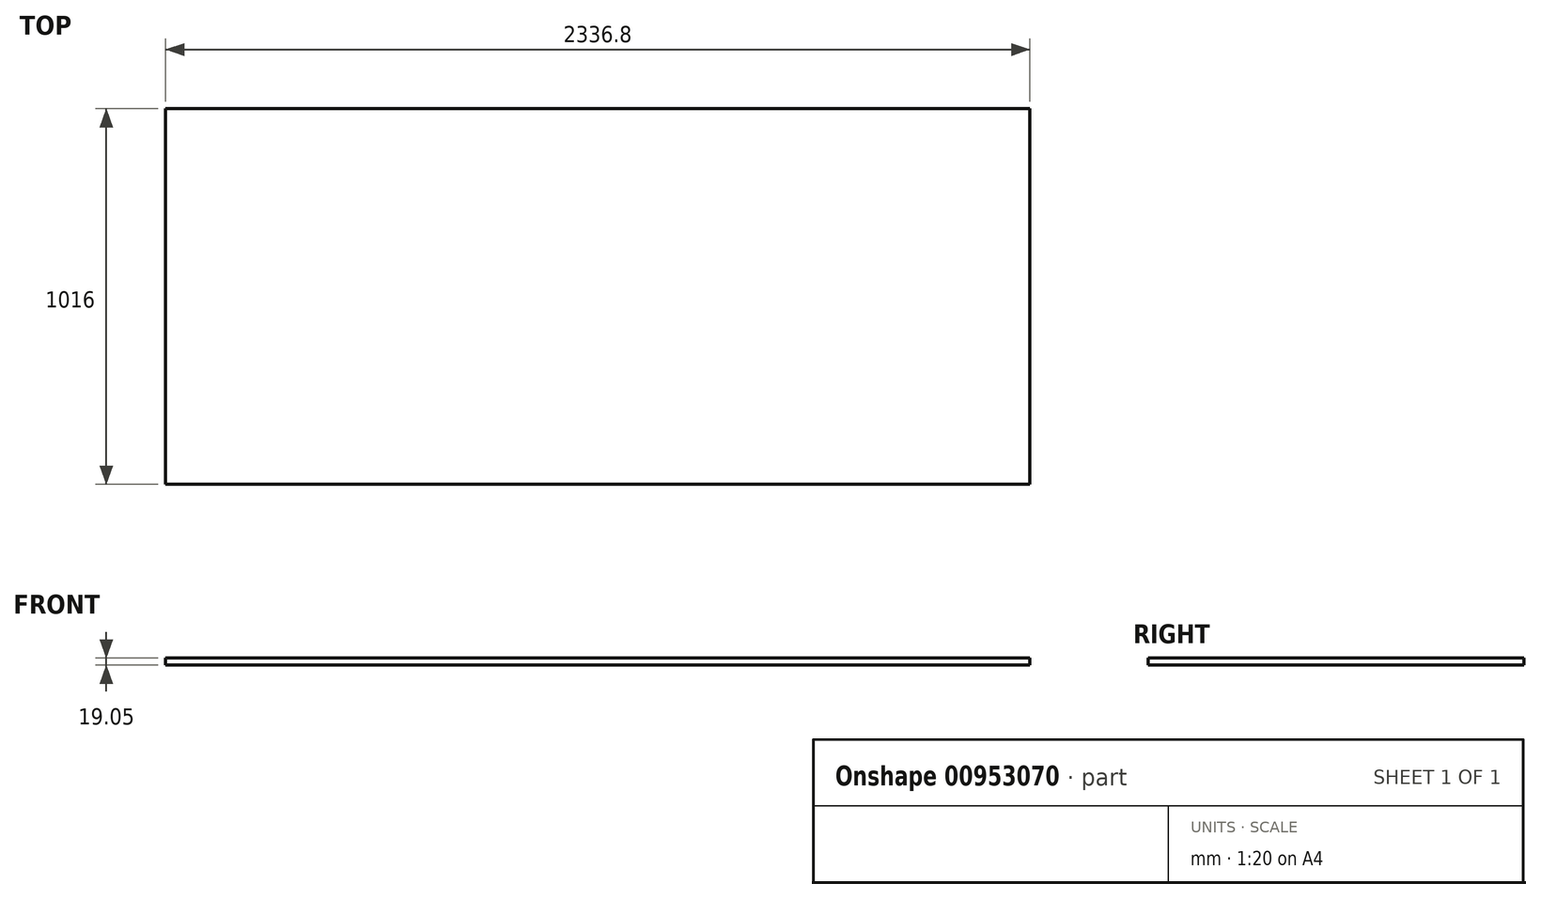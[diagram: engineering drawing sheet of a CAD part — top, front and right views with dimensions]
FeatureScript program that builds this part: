
annotation { "Feature Type Name" : "Feature", "Feature Type Description" : "" }
export const myFeature = defineFeature(function(context is Context, id is Id, definition is map)
    precondition{}
    {
        {
            var Q0;
            Q0=qCreatedBy(makeId("Top.planeOp"),FACE);
            var sketch = newSketch(context, id + "F0", { "sketchPlane" : qUnion([Q0])});
            skLineSegment(sketch, "E0", {"start": v(0, 0) * mm, "end": v(-2336.8, 0) * mm});
            skLineSegment(sketch, "E1", {"start": v(-2336.8, 0) * mm, "end": v(-2336.8, 1016) * mm});
            skLineSegment(sketch, "E2", {"start": v(-2336.8, 1016) * mm, "end": v(0, 1016) * mm});
            skLineSegment(sketch, "E3", {"start": v(0, 1016) * mm, "end": v(0, 0) * mm});
            skSolve(sketch);
        }
        {
            var Q0;
            Q0 = qSketchRegion(id + "F0", true);
            extrude(context, id + "F1", {"entities" : qUnion([Q0]), "depth" : 19.05 * mm, "offsetDistance" : 25.4 * mm});
        }
    });
